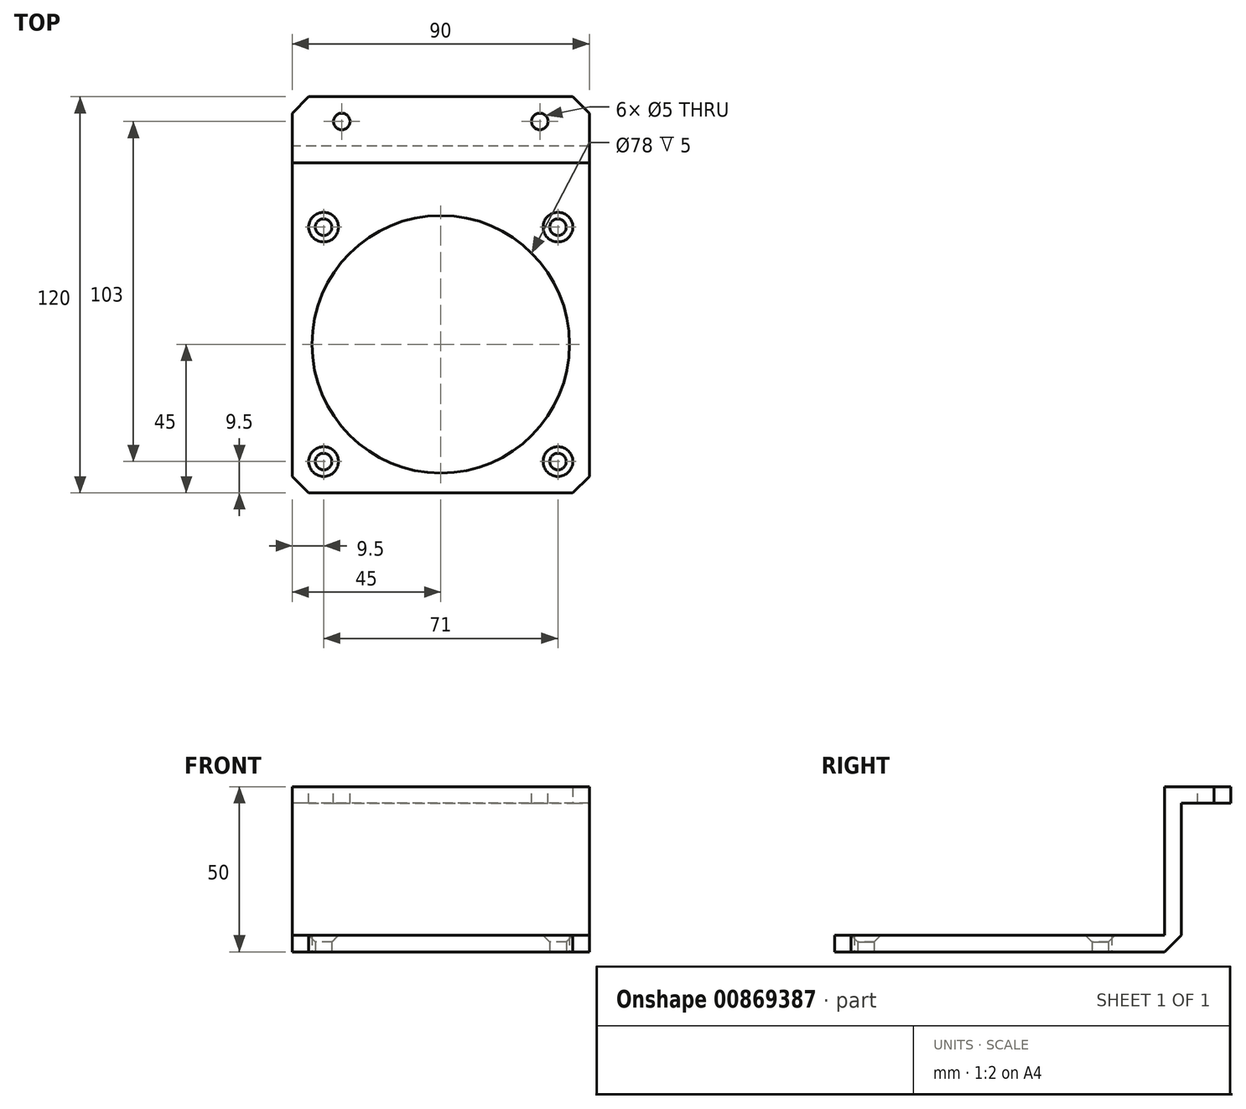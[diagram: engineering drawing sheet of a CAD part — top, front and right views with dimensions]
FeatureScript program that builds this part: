
annotation { "Feature Type Name" : "Feature", "Feature Type Description" : "" }
export const myFeature = defineFeature(function(context is Context, id is Id, definition is map)
    precondition{}
    {
        {
            var Q0;
            Q0=qCreatedBy(makeId("Top.planeOp"),FACE);
            var sketch = newSketch(context, id + "F0", { "sketchPlane" : qUnion([Q0])});
            skLineSegment(sketch, "E0.bottom", {"start": v(-40, 40) * mm, "end": v(40, 40) * mm});
            skLineSegment(sketch, "E0.top", {"start": v(-40, -40) * mm, "end": v(40, -40) * mm});
            skLineSegment(sketch, "E0.left", {"start": v(-40, 40) * mm, "end": v(-40, -40) * mm});
            skLineSegment(sketch, "E0.right", {"start": v(40, 40) * mm, "end": v(40, -40) * mm});
            skCircle(sketch, "E1", {"center": v(-35.5, 35.5) * mm, "radius": 2.5 * mm});
            skCircle(sketch, "E2", {"center": v(35.5, 35.5) * mm, "radius": 2.5 * mm});
            skCircle(sketch, "E3", {"center": v(-35.5, -35.5) * mm, "radius": 2.5 * mm});
            skCircle(sketch, "E4", {"center": v(35.5, -35.5) * mm, "radius": 2.5 * mm});
            skCircle(sketch, "E5", {"center": v(0, 0) * mm, "radius": 39 * mm});
            skLineSegment(sketch, "E6.bottom", {"start": v(-45, 45) * mm, "end": v(45, 45) * mm});
            skLineSegment(sketch, "E6.top", {"start": v(-45, -45) * mm, "end": v(45, -45) * mm});
            skLineSegment(sketch, "E6.left", {"start": v(-45, 45) * mm, "end": v(-45, -45) * mm});
            skLineSegment(sketch, "E6.right", {"start": v(45, 45) * mm, "end": v(45, -45) * mm});
            skLineSegment(sketch, "E7.top", {"start": v(-45, 60) * mm, "end": v(45, 60) * mm});
            skLineSegment(sketch, "E7.left", {"start": v(-45, 45) * mm, "end": v(-45, 60) * mm});
            skLineSegment(sketch, "E7.right", {"start": v(45, 45) * mm, "end": v(45, 60) * mm});
            skLineSegment(sketch, "E8.top", {"start": v(-45, 55) * mm, "end": v(45, 55) * mm});
            skLineSegment(sketch, "E8.left", {"start": v(-45, 60) * mm, "end": v(-45, 55) * mm});
            skLineSegment(sketch, "E8.right", {"start": v(45, 60) * mm, "end": v(45, 55) * mm});
            skSolve(sketch);
        }
        {
            var Q0;
            Q0=makeQuery(id+"F0.imprint","IMPRINT",FACE,{"disambiguationData":[TD([[makeQuery(id+"F0.imprint","IMPRINT",EDGE,{"derivedFrom":sQuery(id+"F0.wireOp",EDGE,"E0.bottom")}),-1.0]])]});
            var Q1;
            Q1=makeQuery(id+"F0.imprint","IMPRINT",FACE,{"disambiguationData":[TD([[makeQuery(id+"F0.imprint","IMPRINT",EDGE,{"derivedFrom":sQuery(id+"F0.wireOp",EDGE,"E0.bottom")}),1.0]])]});
            var Q2;
            {var subQ0=sQuery(id+"F0.wireOp",EDGE,"E6.bottom");Q2=makeQuery(id+"F0.imprint","IMPRINT",FACE,{"disambiguationData":[TD([[makeQuery(id+"F0.imprint","IMPRINT",EDGE,{"derivedFrom":subQ0}),1.0]])]});}
            extrude(context, id + "F1", {"entities" : qUnion([Q0, Q1, Q2]), "depth" : 5 * mm, "offsetDistance" : 25 * mm});
        }
        {
            var Q0;
            {var subQ0=sQuery(id+"F0.wireOp",EDGE,"E7.top");Q0=makeQuery(id+"F0.imprint","IMPRINT",FACE,{"disambiguationData":[TD([[makeQuery(id+"F0.imprint","IMPRINT",EDGE,{"derivedFrom":subQ0}),-1.0]])]});}
            extrude(context, id + "F2", {"entities" : qUnion([Q0]), "operationType" : NewBodyOperationType.ADD, "depth" : 50 * mm, "offsetDistance" : 25 * mm});
        }
        {
            var Q0;
            Q0=makeQuery(id+"F2.opExtrude","SWEPT_FACE",FACE,{"disambiguationData":[OSD([sQuery(id+"F0.wireOp",EDGE,"E8.top")])]});
            var sketch = newSketch(context, id + "F3", { "sketchPlane" : qUnion([Q0])});
            skLineSegment(sketch, "E9.bottom", {"start": v(-45, 50) * mm, "end": v(45, 50) * mm});
            skLineSegment(sketch, "E9.top", {"start": v(-45, 45) * mm, "end": v(45, 45) * mm});
            skLineSegment(sketch, "E9.left", {"start": v(-45, 50) * mm, "end": v(-45, 45) * mm});
            skLineSegment(sketch, "E9.right", {"start": v(45, 50) * mm, "end": v(45, 45) * mm});
            skSolve(sketch);
        }
        {
            var Q0;
            Q0=makeQuery(id+"F3.imprint","IMPRINT",FACE,{"disambiguationData":[TD([[makeQuery(id+"F3.imprint","IMPRINT",EDGE,{"derivedFrom":sQuery(id+"F3.wireOp",EDGE,"E9.bottom")}),-1.0]])]});
            extrude(context, id + "F4", {"entities" : qUnion([Q0]), "operationType" : NewBodyOperationType.ADD, "oppositeDirection" : true, "depth" : 20 * mm, "offsetDistance" : 25 * mm});
        }
        {
            var Q0;
            Q0=makeQuery(id+"F4.boolean.opBoolean","MERGE",FACE,{"derivedFrom":[makeQuery(id+"F2.opExtrude","CAP_FACE",FACE,{"disambiguationData":[OSD([sQuery(id+"F0.wireOp",EDGE,"E7.top"),sQuery(id+"F0.wireOp",EDGE,"E7.left"),sQuery(id+"F0.wireOp",EDGE,"E7.right"),sQuery(id+"F0.wireOp",EDGE,"E8.top")])],"isStart":false}),makeQuery(id+"F4.opExtrude","SWEPT_FACE",FACE,{"disambiguationData":[OSD([sQuery(id+"F3.wireOp",EDGE,"E9.bottom")])]})]});
            var sketch = newSketch(context, id + "F5", { "sketchPlane" : qUnion([Q0])});
            skCircle(sketch, "E10", {"center": v(-30, 67.5) * mm, "radius": 2.5 * mm});
            skCircle(sketch, "E11", {"center": v(30, 67.5) * mm, "radius": 2.5 * mm});
            skSolve(sketch);
        }
        {
            var Q0;
            Q0=makeQuery(id+"F5.imprint","IMPRINT",FACE,{"disambiguationData":[TD([[makeQuery(id+"F5.imprint","IMPRINT",EDGE,{"derivedFrom":sQuery(id+"F5.wireOp",EDGE,"E11")}),1.0]])]});
            var Q1;
            Q1=makeQuery(id+"F5.imprint","IMPRINT",FACE,{"disambiguationData":[TD([[makeQuery(id+"F5.imprint","IMPRINT",EDGE,{"derivedFrom":sQuery(id+"F5.wireOp",EDGE,"E10")}),1.0]])]});
            extrude(context, id + "F6", {"entities" : qUnion([Q0, Q1]), "operationType" : NewBodyOperationType.REMOVE, "oppositeDirection" : true, "depth" : 10 * mm, "offsetDistance" : 25 * mm});
        }
        {
            var Q0;
            Q0=makeQuery(id+"F1.opExtrude","SWEPT_EDGE",EDGE,{"disambiguationData":[OSD([sQuery(id+"F0.wireOp",EDGE,"E6.top"),sQuery(id+"F0.wireOp",EDGE,"E6.left")])]});
            var Q1;
            Q1=makeQuery(id+"F1.opExtrude","SWEPT_EDGE",EDGE,{"disambiguationData":[OSD([sQuery(id+"F0.wireOp",EDGE,"E6.top"),sQuery(id+"F0.wireOp",EDGE,"E6.right")])]});
            var Q2;
            Q2=makeQuery(id+"F4.opExtrude","CAP_EDGE",EDGE,{"disambiguationData":[OSD([sQuery(id+"F3.wireOp",EDGE,"E9.right")])],"isStart":false});
            var Q3;
            Q3=makeQuery(id+"F4.opExtrude","CAP_EDGE",EDGE,{"disambiguationData":[OSD([sQuery(id+"F3.wireOp",EDGE,"E9.left")])],"isStart":false});
            var Q4;
            Q4=makeQuery(id+"F1.opExtrude","CAP_EDGE",EDGE,{"disambiguationData":[OSD([sQuery(id+"F0.wireOp",EDGE,"E8.top")])],"isStart":false});
            var Q5;
            Q5=makeQuery(id+"F2.opExtrude","CAP_EDGE",EDGE,{"disambiguationData":[OSD([sQuery(id+"F0.wireOp",EDGE,"E7.top")])],"isStart":true});
            chamfer(context, id + "F7", {"entities" : qUnion([Q0, Q1, Q2, Q3, Q4, Q5]), "width" : 5 * mm, "tangentPropagation" : true});
        }
        {
            var Q0;
            Q0=makeQuery(id+"F1.opExtrude","CAP_EDGE",EDGE,{"disambiguationData":[OSD([sQuery(id+"F0.wireOp",EDGE,"E3")])],"isStart":false});
            var Q1;
            Q1=makeQuery(id+"F1.opExtrude","CAP_EDGE",EDGE,{"disambiguationData":[OSD([sQuery(id+"F0.wireOp",EDGE,"E4")])],"isStart":false});
            var Q2;
            Q2=makeQuery(id+"F1.opExtrude","CAP_EDGE",EDGE,{"disambiguationData":[OSD([sQuery(id+"F0.wireOp",EDGE,"E2")])],"isStart":false});
            var Q3;
            Q3=makeQuery(id+"F1.opExtrude","CAP_EDGE",EDGE,{"disambiguationData":[OSD([sQuery(id+"F0.wireOp",EDGE,"E1")])],"isStart":false});
            chamfer(context, id + "F8", {"entities" : qUnion([Q0, Q1, Q2, Q3]), "width" : 2 * mm, "tangentPropagation" : true});
        }
    });
